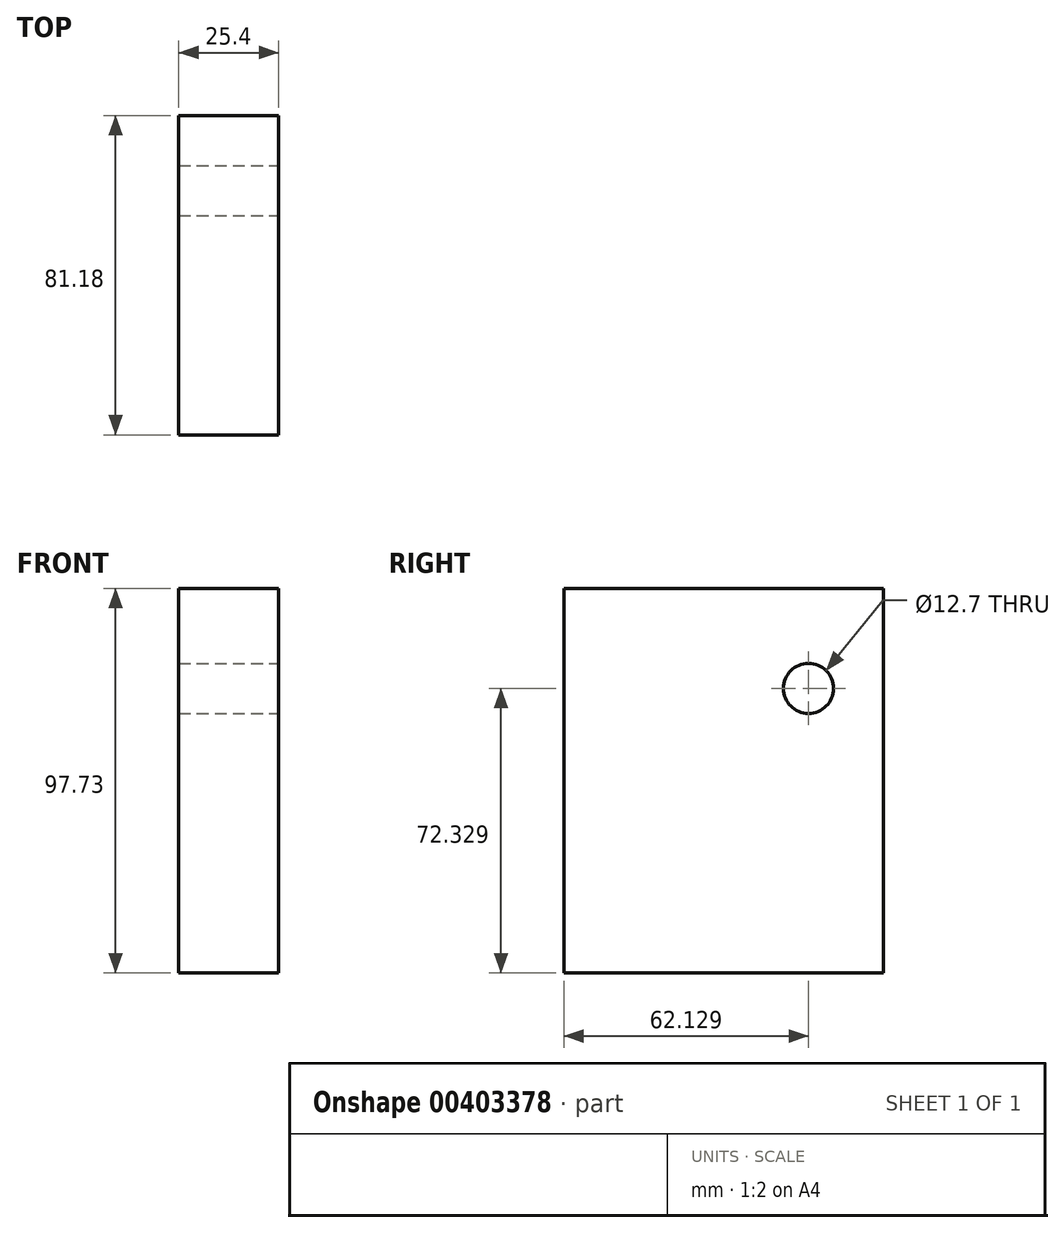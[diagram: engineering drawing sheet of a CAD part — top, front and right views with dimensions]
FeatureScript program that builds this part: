
annotation { "Feature Type Name" : "Feature", "Feature Type Description" : "" }
export const myFeature = defineFeature(function(context is Context, id is Id, definition is map)
    precondition{}
    {
        {
            var Q0;
            Q0=qCreatedBy(makeId("Right.planeOp"),FACE);
            var sketch = newSketch(context, id + "F0", { "sketchPlane" : qUnion([Q0])});
            skLineSegment(sketch, "E0.bottom", {"start": v(-37.83, 46.7) * mm, "end": v(43.35, 46.7) * mm});
            skLineSegment(sketch, "E0.top", {"start": v(-37.83, -51.03) * mm, "end": v(43.35, -51.03) * mm});
            skLineSegment(sketch, "E0.left", {"start": v(-37.83, 46.7) * mm, "end": v(-37.83, -51.03) * mm});
            skLineSegment(sketch, "E0.right", {"start": v(43.35, 46.7) * mm, "end": v(43.35, -51.03) * mm});
            skSolve(sketch);
        }
        {
            var Q0;
            Q0=makeQuery(id+"F0.imprint","IMPRINT",FACE,{"disambiguationData":[TD([[makeQuery(id+"F0.imprint","IMPRINT",EDGE,{"derivedFrom":sQuery(id+"F0.wireOp",EDGE,"E0.bottom")}),-1.0]])]});
            extrude(context, id + "F1", {"entities" : qUnion([Q0]), "endBound" : BoundingType.SYMMETRIC, "depth" : 25.4 * mm});
        }
        {
            var Q0;
            Q0=makeQuery(id+"F1.opExtrude","CAP_FACE",FACE,{"disambiguationData":[OSD([sQuery(id+"F0.wireOp",EDGE,"E0.bottom"),sQuery(id+"F0.wireOp",EDGE,"E0.top"),sQuery(id+"F0.wireOp",EDGE,"E0.left"),sQuery(id+"F0.wireOp",EDGE,"E0.right")])],"isStart":false});
            var sketch = newSketch(context, id + "F2", { "sketchPlane" : qUnion([Q0])});
            skPoint(sketch, "E1", {"position": v(24.3, 21.3) * mm});
            skSolve(sketch);
        }
        {
            var Q0;
            Q0=sQuery(id+"F2.wireOp",VERTEX,"E1");
            var Q1;
            Q1=makeQuery(id+"F1.opExtrude","SWEPT_BODY",BODY,{"disambiguationData":[OSD([sQuery(id+"F0.wireOp",EDGE,"E0.bottom"),sQuery(id+"F0.wireOp",EDGE,"E0.top"),sQuery(id+"F0.wireOp",EDGE,"E0.left"),sQuery(id+"F0.wireOp",EDGE,"E0.right")])]});
            hole(context, id + "F3", {"style" : HoleStyle.SIMPLE, "endStyle" : HoleEndStyle.THROUGH, "holeDiameter" : 12.7 * mm, "isTappedThrough" : true, "tappedDepth" : 12.7 * mm, "tapClearance" : 3, "locations" : qUnion([Q0]), "scope" : qUnion([Q1])});
        }
    });
